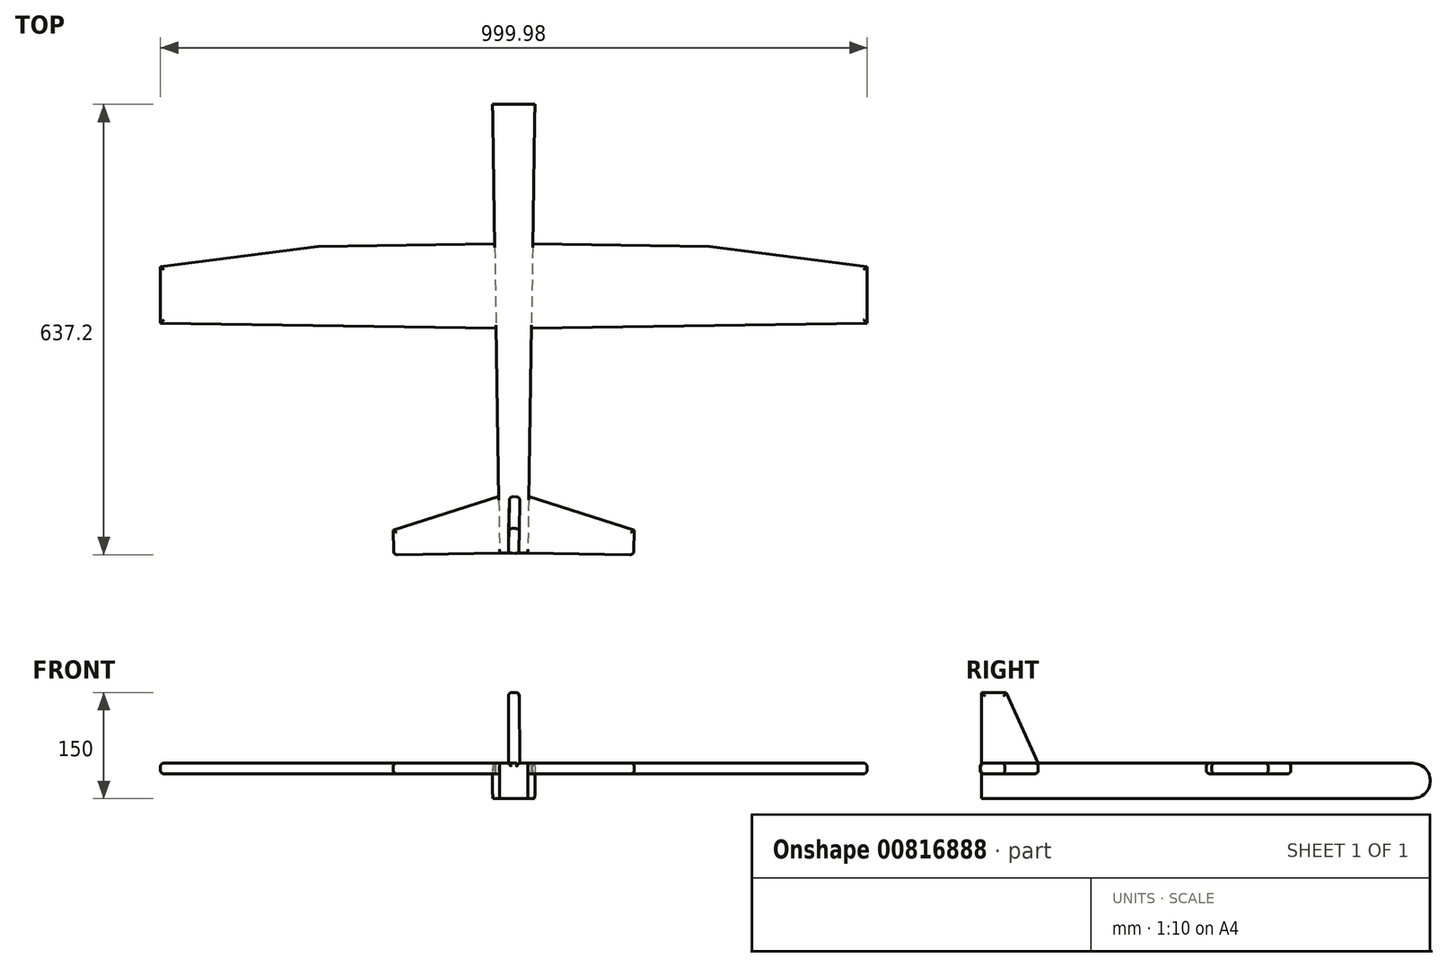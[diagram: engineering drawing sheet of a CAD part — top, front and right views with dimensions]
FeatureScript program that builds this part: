
annotation { "Feature Type Name" : "Feature", "Feature Type Description" : "" }
export const myFeature = defineFeature(function(context is Context, id is Id, definition is map)
    precondition{}
    {
        {
            var Q0;
            Q0=qCreatedBy(makeId("Top.planeOp"),FACE);
            var sketch = newSketch(context, id + "F0", { "sketchPlane" : qUnion([Q0])});
            skLineSegment(sketch, "E0", {"start": v(-30, 317.46) * mm, "end": v(-20, -317.46) * mm});
            skLineSegment(sketch, "E1", {"start": v(30, 317.46) * mm, "end": v(20, -317.46) * mm});
            skLineSegment(sketch, "E2", {"start": v(0, -317.46) * mm, "end": v(0, 317.46) * mm, "construction": true});
            skLineSegment(sketch, "E3", {"start": v(-20, -317.46) * mm, "end": v(20, -317.46) * mm});
            skLineSegment(sketch, "E4", {"start": v(-30, 317.46) * mm, "end": v(30, 317.46) * mm});
            skLineSegment(sketch, "E5", {"start": v(0, 0) * mm, "end": v(-499.94, 7.87) * mm});
            skLineSegment(sketch, "E6", {"start": v(-500, 87.87) * mm, "end": v(-499.94, 7.87) * mm});
            skLineSegment(sketch, "E7.MirrorCS", {"start": v(500, 87.87) * mm, "end": v(499.94, 7.87) * mm});
            skLineSegment(sketch, "E8.MirrorCS", {"start": v(0, 0) * mm, "end": v(499.94, 7.87) * mm});
            skLineSegment(sketch, "E9", {"start": v(-20, -317.46) * mm, "end": v(-169.98, -319.82) * mm});
            skLineSegment(sketch, "E10", {"start": v(-169.98, -319.82) * mm, "end": v(-170.53, -284.83) * mm});
            skLineSegment(sketch, "E11", {"start": v(-170.53, -284.83) * mm, "end": v(-21.26, -237.46) * mm});
            skLineSegment(sketch, "E12.MirrorCS", {"start": v(20, -317.46) * mm, "end": v(169.98, -319.82) * mm});
            skLineSegment(sketch, "E13.MirrorCS", {"start": v(169.98, -319.82) * mm, "end": v(170.53, -284.83) * mm});
            skLineSegment(sketch, "E14.MirrorCS", {"start": v(170.53, -284.83) * mm, "end": v(21.26, -237.46) * mm});
            skLineSegment(sketch, "E15", {"start": v(-26.89, 120) * mm, "end": v(-276.89, 116.06) * mm});
            skLineSegment(sketch, "E16", {"start": v(-276.89, 116.06) * mm, "end": v(-500, 87.87) * mm});
            skLineSegment(sketch, "E17.MirrorCS", {"start": v(26.89, 120) * mm, "end": v(276.89, 116.06) * mm});
            skLineSegment(sketch, "E18.MirrorCS", {"start": v(276.89, 116.06) * mm, "end": v(500, 87.87) * mm});
            skSolve(sketch);
        }
        {
            var Q0;
            {var subQ0=sQuery(id+"F0.wireOp",EDGE,"E4");Q0=makeQuery(id+"F0.imprint","IMPRINT",FACE,{"disambiguationData":[TD([[makeQuery(id+"F0.imprint","IMPRINT",EDGE,{"derivedFrom":subQ0}),-1.0]])]});}
            var Q1;
            {var subQ1=sQuery(id+"F0.wireOp",EDGE,"qLZcTgty-8P5V-7AuH-MDfv-ml2M47v9YugA");var subQ3=sQuery(id+"F0.wireOp",EDGE,"E0");var subQ4=makeQuery(id+"F0.imprint","INTERSECT",VERTEX,{"derivedFrom":[subQ3,subQ1]});Q1=makeQuery(id+"F0.imprint","IMPRINT",FACE,{"disambiguationData":[TD([[makeQuery(id+"F0.imprint","IMPRINT",EDGE,{"disambiguationData":[TD([[subQ4,-1.0]])],"derivedFrom":subQ3}),1.0]])]});}
            var Q2;
            {var subQ5=sQuery(id+"F0.wireOp",EDGE,"E3");Q2=makeQuery(id+"F0.imprint","IMPRINT",FACE,{"disambiguationData":[TD([[makeQuery(id+"F0.imprint","IMPRINT",EDGE,{"derivedFrom":subQ5}),1.0]])]});}
            extrude(context, id + "F1", {"entities" : qUnion([Q0, Q1, Q2]), "oppositeDirection" : true, "depth" : 50 * mm, "offsetDistance" : 25 * mm});
        }
        {
            var Q0;
            {var subQ5=sQuery(id+"F0.wireOp",EDGE,"E6");Q0=makeQuery(id+"F0.imprint","IMPRINT",FACE,{"disambiguationData":[TD([[makeQuery(id+"F0.imprint","IMPRINT",EDGE,{"derivedFrom":subQ5}),1.0]])]});}
            var Q1;
            {var subQ5=sQuery(id+"F0.wireOp",EDGE,"E7.MirrorCS");Q1=makeQuery(id+"F0.imprint","IMPRINT",FACE,{"disambiguationData":[TD([[makeQuery(id+"F0.imprint","IMPRINT",EDGE,{"derivedFrom":subQ5}),-1.0]])]});}
            extrude(context, id + "F2", {"entities" : qUnion([Q0, Q1]), "operationType" : NewBodyOperationType.ADD, "oppositeDirection" : true, "depth" : 15 * mm, "offsetDistance" : 25 * mm});
        }
        {
            var Q0;
            Q0=makeQuery(id+"F1.opExtrude","SWEPT_FACE",FACE,{"disambiguationData":[OSD([sQuery(id+"F0.wireOp",EDGE,"E1")])]});
            cPlane(context, id + "F3", {"entities" : qUnion([Q0]), "cplaneType" : CPlaneType.OFFSET, "offset" : 20 * mm, "oppositeDirection" : true, "width" : 150 * mm, "height" : 150 * mm});
        }
        {
            var Q0;
            Q0=qCreatedBy(id+"F3.planeOp",FACE);
            var sketch = newSketch(context, id + "F4", { "sketchPlane" : qUnion([Q0])});
            skLineSegment(sketch, "E19", {"start": v(-317.74, 0) * mm, "end": v(-317.74, 100) * mm});
            skLineSegment(sketch, "E20", {"start": v(-317.74, 100) * mm, "end": v(-282.74, 100) * mm});
            skLineSegment(sketch, "E21", {"start": v(-282.74, 100) * mm, "end": v(-237.74, 0) * mm});
            skLineSegment(sketch, "E22", {"start": v(-317.74, 0) * mm, "end": v(-237.74, 0) * mm});
            skSolve(sketch);
        }
        {
            var Q0;
            {var subQ0=sQuery(id+"F0.wireOp",EDGE,"E12.MirrorCS");Q0=makeQuery(id+"F0.imprint","IMPRINT",FACE,{"disambiguationData":[TD([[makeQuery(id+"F0.imprint","IMPRINT",EDGE,{"derivedFrom":subQ0}),1.0]])]});}
            var Q1;
            {var subQ0=sQuery(id+"F0.wireOp",EDGE,"E9");Q1=makeQuery(id+"F0.imprint","IMPRINT",FACE,{"disambiguationData":[TD([[makeQuery(id+"F0.imprint","IMPRINT",EDGE,{"derivedFrom":subQ0}),-1.0]])]});}
            extrude(context, id + "F5", {"entities" : qUnion([Q0, Q1]), "operationType" : NewBodyOperationType.ADD, "oppositeDirection" : true, "depth" : 15 * mm, "offsetDistance" : 25 * mm});
        }
        {
            var Q0;
            Q0=makeQuery(id+"F4.imprint","IMPRINT",FACE,{"disambiguationData":[TD([[makeQuery(id+"F4.imprint","IMPRINT",EDGE,{"derivedFrom":sQuery(id+"F4.wireOp",EDGE,"E19")}),-1.0]])]});
            extrude(context, id + "F6", {"entities" : qUnion([Q0]), "operationType" : NewBodyOperationType.ADD, "endBound" : BoundingType.SYMMETRIC, "depth" : 15 * mm, "offsetDistance" : 25 * mm});
        }
        {
            var Q0;
            Q0=makeQuery(id+"F1.opExtrude","CAP_EDGE",EDGE,{"disambiguationData":[OSD([sQuery(id+"F0.wireOp",EDGE,"E4")])],"isStart":true});
            var Q1;
            Q1=makeQuery(id+"F1.opExtrude","CAP_EDGE",EDGE,{"disambiguationData":[OSD([sQuery(id+"F0.wireOp",EDGE,"E4")])],"isStart":false});
            fillet(context, id + "F7", {"entities" : qUnion([Q0, Q1]), "radius" : 25 * mm, "tangentPropagation" : true, "allowEdgeOverflow" : false});
        }
        {
            var Q0;
            Q0=makeQuery(id+"F2.opExtrude","CAP_EDGE",EDGE,{"disambiguationData":[OSD([sQuery(id+"F0.wireOp",EDGE,"E18.MirrorCS")])],"isStart":true});
            var Q1;
            Q1=makeQuery(id+"F2.opExtrude","CAP_EDGE",EDGE,{"disambiguationData":[OSD([sQuery(id+"F0.wireOp",EDGE,"E17.MirrorCS")])],"isStart":true});
            var Q2;
            Q2=makeQuery(id+"F2.opExtrude","CAP_EDGE",EDGE,{"disambiguationData":[OSD([sQuery(id+"F0.wireOp",EDGE,"E17.MirrorCS")])],"isStart":false});
            var Q3;
            Q3=makeQuery(id+"F2.opExtrude","CAP_EDGE",EDGE,{"disambiguationData":[OSD([sQuery(id+"F0.wireOp",EDGE,"E18.MirrorCS")])],"isStart":false});
            var Q4;
            Q4=makeQuery(id+"F2.opExtrude","CAP_EDGE",EDGE,{"disambiguationData":[OSD([sQuery(id+"F0.wireOp",EDGE,"E15")])],"isStart":true});
            var Q5;
            Q5=makeQuery(id+"F2.opExtrude","CAP_EDGE",EDGE,{"disambiguationData":[OSD([sQuery(id+"F0.wireOp",EDGE,"E15")])],"isStart":false});
            var Q6;
            Q6=makeQuery(id+"F2.opExtrude","CAP_EDGE",EDGE,{"disambiguationData":[OSD([sQuery(id+"F0.wireOp",EDGE,"E16")])],"isStart":true});
            var Q7;
            Q7=makeQuery(id+"F2.opExtrude","CAP_EDGE",EDGE,{"disambiguationData":[OSD([sQuery(id+"F0.wireOp",EDGE,"E16")])],"isStart":false});
            var Q8;
            Q8=makeQuery(id+"F2.opExtrude","CAP_EDGE",EDGE,{"disambiguationData":[OSD([sQuery(id+"F0.wireOp",EDGE,"E6")])],"isStart":true});
            var Q9;
            Q9=makeQuery(id+"F2.opExtrude","CAP_EDGE",EDGE,{"disambiguationData":[OSD([sQuery(id+"F0.wireOp",EDGE,"E7.MirrorCS")])],"isStart":true});
            var Q10;
            Q10=makeQuery(id+"F2.opExtrude","CAP_EDGE",EDGE,{"disambiguationData":[OSD([sQuery(id+"F0.wireOp",EDGE,"E6")])],"isStart":false});
            var Q11;
            Q11=makeQuery(id+"F2.opExtrude","CAP_EDGE",EDGE,{"disambiguationData":[OSD([sQuery(id+"F0.wireOp",EDGE,"E5")])],"isStart":true});
            var Q12;
            Q12=makeQuery(id+"F2.opExtrude","CAP_EDGE",EDGE,{"disambiguationData":[OSD([sQuery(id+"F0.wireOp",EDGE,"E8.MirrorCS")])],"isStart":true});
            var Q13;
            Q13=makeQuery(id+"F2.opExtrude","CAP_EDGE",EDGE,{"disambiguationData":[OSD([sQuery(id+"F0.wireOp",EDGE,"E8.MirrorCS")])],"isStart":false});
            var Q14;
            Q14=makeQuery(id+"F2.opExtrude","CAP_EDGE",EDGE,{"disambiguationData":[OSD([sQuery(id+"F0.wireOp",EDGE,"E5")])],"isStart":false});
            var Q15;
            Q15=makeQuery(id+"F2.opExtrude","CAP_EDGE",EDGE,{"disambiguationData":[OSD([sQuery(id+"F0.wireOp",EDGE,"E7.MirrorCS")])],"isStart":false});
            fillet(context, id + "F8", {"entities" : qUnion([Q0, Q1, Q2, Q3, Q4, Q5, Q6, Q7, Q8, Q9, Q10, Q11, Q12, Q13, Q14, Q15]), "radius" : 5 * mm, "tangentPropagation" : true, "allowEdgeOverflow" : false});
        }
        {
            var Q0;
            Q0=makeQuery(id+"F5.opExtrude","CAP_EDGE",EDGE,{"disambiguationData":[OSD([sQuery(id+"F0.wireOp",EDGE,"E13.MirrorCS")])],"isStart":true});
            var Q1;
            Q1=makeQuery(id+"F5.opExtrude","CAP_EDGE",EDGE,{"disambiguationData":[OSD([sQuery(id+"F0.wireOp",EDGE,"E13.MirrorCS")])],"isStart":false});
            var Q2;
            Q2=makeQuery(id+"F5.opExtrude","CAP_EDGE",EDGE,{"disambiguationData":[OSD([sQuery(id+"F0.wireOp",EDGE,"E12.MirrorCS")])],"isStart":false});
            var Q3;
            Q3=makeQuery(id+"F6.opExtrude","CAP_EDGE",EDGE,{"disambiguationData":[OSD([sQuery(id+"F4.wireOp",EDGE,"E19")])],"isStart":false});
            var Q4;
            Q4=makeQuery(id+"F5.opExtrude","CAP_EDGE",EDGE,{"disambiguationData":[OSD([sQuery(id+"F0.wireOp",EDGE,"E14.MirrorCS")])],"isStart":true});
            var Q5;
            Q5=makeQuery(id+"F5.opExtrude","CAP_EDGE",EDGE,{"disambiguationData":[OSD([sQuery(id+"F0.wireOp",EDGE,"E14.MirrorCS")])],"isStart":false});
            var Q6;
            Q6=makeQuery(id+"F5.opExtrude","CAP_EDGE",EDGE,{"disambiguationData":[OSD([sQuery(id+"F0.wireOp",EDGE,"E11")])],"isStart":false});
            var Q7;
            Q7=makeQuery(id+"F5.opExtrude","CAP_EDGE",EDGE,{"disambiguationData":[OSD([sQuery(id+"F0.wireOp",EDGE,"E9")])],"isStart":false});
            var Q8;
            Q8=makeQuery(id+"F5.opExtrude","CAP_EDGE",EDGE,{"disambiguationData":[OSD([sQuery(id+"F0.wireOp",EDGE,"E10")])],"isStart":false});
            var Q9;
            Q9=makeQuery(id+"F5.opExtrude","CAP_EDGE",EDGE,{"disambiguationData":[OSD([sQuery(id+"F0.wireOp",EDGE,"E10")])],"isStart":true});
            var Q10;
            Q10=makeQuery(id+"F5.opExtrude","CAP_EDGE",EDGE,{"disambiguationData":[OSD([sQuery(id+"F0.wireOp",EDGE,"E11")])],"isStart":true});
            var Q11;
            Q11=makeQuery(id+"F6.opExtrude","CAP_EDGE",EDGE,{"disambiguationData":[OSD([sQuery(id+"F4.wireOp",EDGE,"E19")])],"isStart":true});
            var Q12;
            Q12=makeQuery(id+"F6.opExtrude","CAP_EDGE",EDGE,{"disambiguationData":[OSD([sQuery(id+"F4.wireOp",EDGE,"E21")])],"isStart":true});
            var Q13;
            Q13=makeQuery(id+"F6.opExtrude","CAP_EDGE",EDGE,{"disambiguationData":[OSD([sQuery(id+"F4.wireOp",EDGE,"E21")])],"isStart":false});
            var Q14;
            Q14=makeQuery(id+"F6.opExtrude","CAP_EDGE",EDGE,{"disambiguationData":[OSD([sQuery(id+"F4.wireOp",EDGE,"E20")])],"isStart":true});
            var Q15;
            Q15=makeQuery(id+"F6.opExtrude","CAP_EDGE",EDGE,{"disambiguationData":[OSD([sQuery(id+"F4.wireOp",EDGE,"E20")])],"isStart":false});
            fillet(context, id + "F9", {"entities" : qUnion([Q0, Q1, Q2, Q3, Q4, Q5, Q6, Q7, Q8, Q9, Q10, Q11, Q12, Q13, Q14, Q15]), "radius" : 5 * mm, "tangentPropagation" : true, "allowEdgeOverflow" : false});
        }
        {
            var Q0;
            Q0=makeQuery(id+"F2.opExtrude","SWEPT_EDGE",EDGE,{"disambiguationData":[OSD([sQuery(id+"F0.wireOp",EDGE,"E17.MirrorCS"),sQuery(id+"F0.wireOp",EDGE,"E18.MirrorCS")])]});
            var Q1;
            Q1=makeQuery(id+"F2.opExtrude","SWEPT_EDGE",EDGE,{"disambiguationData":[OSD([sQuery(id+"F0.wireOp",EDGE,"E15"),sQuery(id+"F0.wireOp",EDGE,"E16")])]});
            var Q2;
            Q2=makeQuery(id+"F8.opFillet","BLEND_EDGE",EDGE,{"blendedFrom":[makeQuery(id+"F2.opExtrude","CAP_EDGE",EDGE,{"disambiguationData":[OSD([sQuery(id+"F0.wireOp",EDGE,"E17.MirrorCS")])],"isStart":true}),makeQuery(id+"F2.opExtrude","CAP_EDGE",EDGE,{"disambiguationData":[OSD([sQuery(id+"F0.wireOp",EDGE,"E18.MirrorCS")])],"isStart":true})],"blendedInto":[]});
            var Q3;
            Q3=makeQuery(id+"F8.opFillet","BLEND_EDGE",EDGE,{"blendedFrom":[makeQuery(id+"F2.opExtrude","CAP_EDGE",EDGE,{"disambiguationData":[OSD([sQuery(id+"F0.wireOp",EDGE,"E15")])],"isStart":true}),makeQuery(id+"F2.opExtrude","CAP_EDGE",EDGE,{"disambiguationData":[OSD([sQuery(id+"F0.wireOp",EDGE,"E16")])],"isStart":true})],"blendedInto":[]});
            var Q4;
            Q4=makeQuery(id+"F8.opFillet","BLEND_EDGE",EDGE,{"blendedFrom":[makeQuery(id+"F2.opExtrude","CAP_EDGE",EDGE,{"disambiguationData":[OSD([sQuery(id+"F0.wireOp",EDGE,"E17.MirrorCS")])],"isStart":false}),makeQuery(id+"F2.opExtrude","CAP_EDGE",EDGE,{"disambiguationData":[OSD([sQuery(id+"F0.wireOp",EDGE,"E18.MirrorCS")])],"isStart":false})],"blendedInto":[]});
            var Q5;
            Q5=makeQuery(id+"F8.opFillet","BLEND_EDGE",EDGE,{"blendedFrom":[makeQuery(id+"F2.opExtrude","CAP_EDGE",EDGE,{"disambiguationData":[OSD([sQuery(id+"F0.wireOp",EDGE,"E15")])],"isStart":false}),makeQuery(id+"F2.opExtrude","CAP_EDGE",EDGE,{"disambiguationData":[OSD([sQuery(id+"F0.wireOp",EDGE,"E16")])],"isStart":false})],"blendedInto":[]});
            var Q6;
            Q6=makeQuery(id+"F5.opExtrude","CAP_EDGE",EDGE,{"disambiguationData":[OSD([sQuery(id+"F0.wireOp",EDGE,"E9")])],"isStart":true});
            var Q7;
            Q7=makeQuery(id+"F5.opExtrude","CAP_EDGE",EDGE,{"disambiguationData":[OSD([sQuery(id+"F0.wireOp",EDGE,"E12.MirrorCS")])],"isStart":true});
            fillet(context, id + "F10", {"entities" : qUnion([Q0, Q1, Q2, Q3, Q4, Q5, Q6, Q7]), "radius" : 5 * mm, "tangentPropagation" : true, "allowEdgeOverflow" : false});
        }
    });
